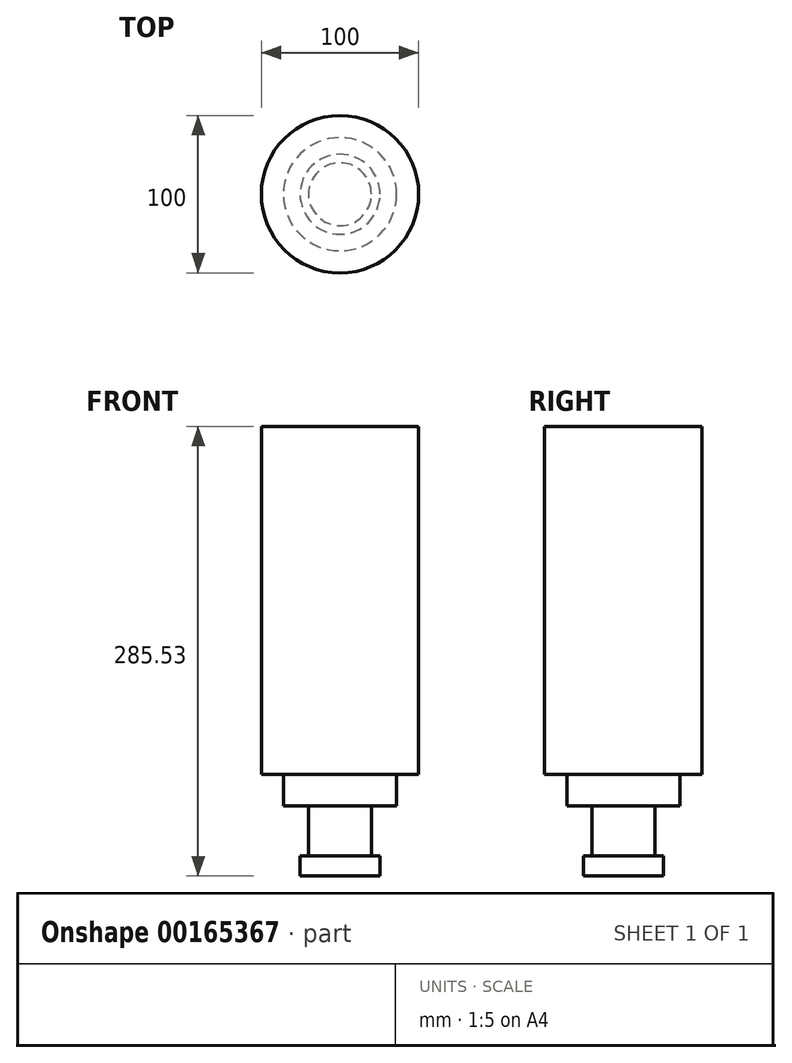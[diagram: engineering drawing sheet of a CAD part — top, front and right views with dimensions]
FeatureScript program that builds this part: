
annotation { "Feature Type Name" : "Feature", "Feature Type Description" : "" }
export const myFeature = defineFeature(function(context is Context, id is Id, definition is map)
    precondition{}
    {
        {
            var Q0;
            Q0=qCreatedBy(makeId("Top.planeOp"),FACE);
            var sketch = newSketch(context, id + "F0", { "sketchPlane" : qUnion([Q0])});
            skCircle(sketch, "E0", {"center": v(0, 0) * mm, "radius": 25.4 * mm});
            skSolve(sketch);
        }
        {
            var Q0;
            Q0=qSketchRegion(id+"F0",true);
            extrude(context, id + "F1", {"entities" : qUnion([Q0]), "depth" : 12.7 * mm});
        }
        {
            var Q0;
            Q0=makeQuery(id+"F1.opExtrude","CAP_FACE",FACE,{"disambiguationData":[OSD([sQuery(id+"F0.wireOp",EDGE,"E0")])],"isStart":false});
            var sketch = newSketch(context, id + "F2", { "sketchPlane" : qUnion([Q0])});
            skCircle(sketch, "E1", {"center": v(0, 0) * mm, "radius": 19.94 * mm});
            skSolve(sketch);
        }
        {
            var Q0;
            Q0=qSketchRegion(id+"F2",true);
            extrude(context, id + "F3", {"entities" : qUnion([Q0]), "operationType" : NewBodyOperationType.ADD, "depth" : 31.75 * mm});
        }
        {
            var Q0;
            Q0=makeQuery(id+"F3.opExtrude","CAP_FACE",FACE,{"disambiguationData":[OSD([sQuery(id+"F2.wireOp",EDGE,"E1")])],"isStart":false});
            var sketch = newSketch(context, id + "F4", { "sketchPlane" : qUnion([Q0])});
            skCircle(sketch, "E2", {"center": v(0, 0) * mm, "radius": 36 * mm});
            skSolve(sketch);
        }
        {
            var Q0;
            Q0=qSketchRegion(id+"F4",true);
            extrude(context, id + "F5", {"entities" : qUnion([Q0]), "operationType" : NewBodyOperationType.ADD, "depth" : 20 * mm});
        }
        {
            var Q0;
            Q0=makeQuery(id+"F5.opExtrude","CAP_FACE",FACE,{"disambiguationData":[OSD([sQuery(id+"F4.wireOp",EDGE,"E2")])],"isStart":false});
            var sketch = newSketch(context, id + "F6", { "sketchPlane" : qUnion([Q0])});
            skCircle(sketch, "E3", {"center": v(0, 0) * mm, "radius": 50 * mm});
            skSolve(sketch);
        }
        {
            var Q0;
            Q0=qSketchRegion(id+"F6",true);
            extrude(context, id + "F7", {"entities" : qUnion([Q0]), "operationType" : NewBodyOperationType.ADD, "depth" : 221.08 * mm});
        }
    });
